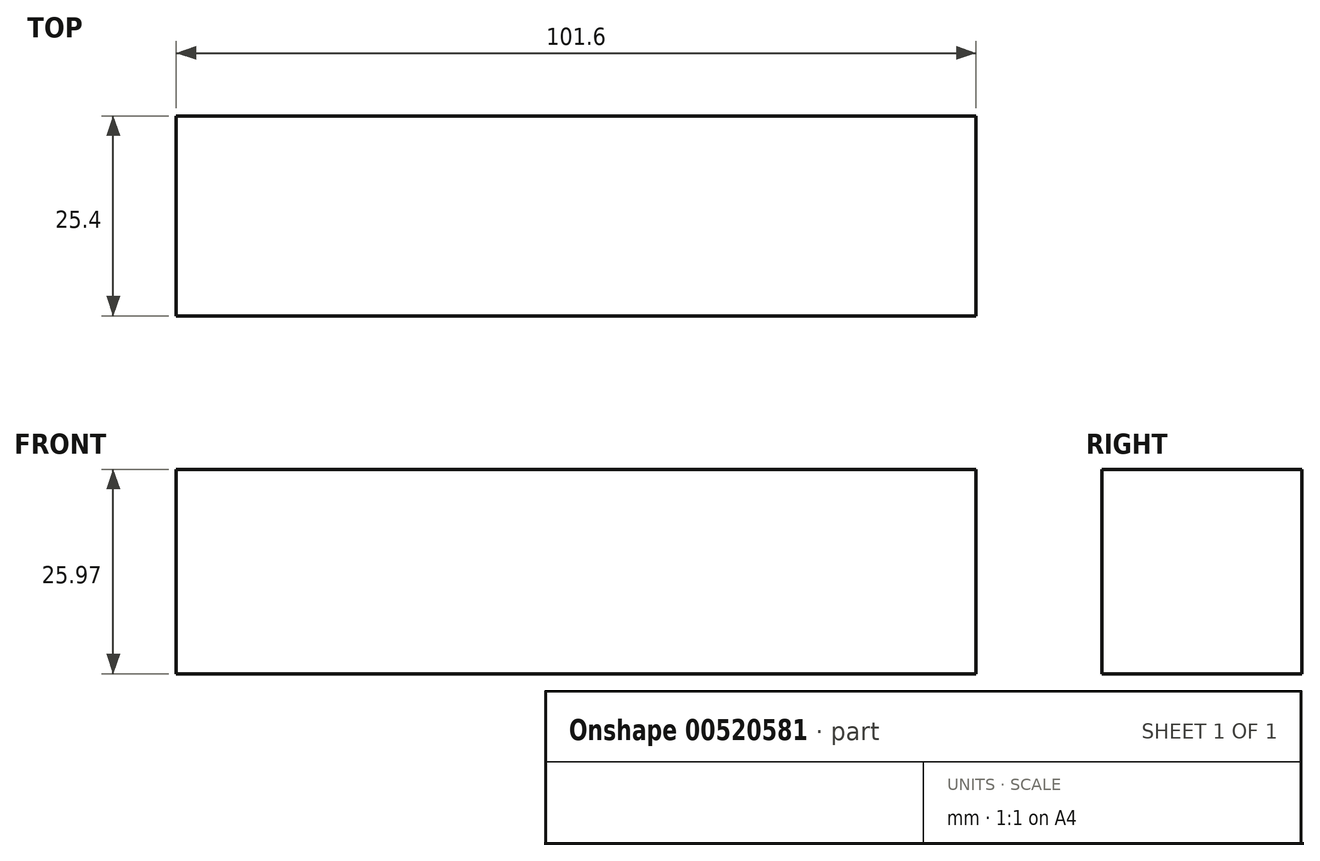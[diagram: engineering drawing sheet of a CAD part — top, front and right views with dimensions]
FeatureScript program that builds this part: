
annotation { "Feature Type Name" : "Feature", "Feature Type Description" : "" }
export const myFeature = defineFeature(function(context is Context, id is Id, definition is map)
    precondition{}
    {
        {
            var Q0;
            Q0=qCreatedBy(makeId("Front.planeOp"),FACE);
            var sketch = newSketch(context, id + "F0", { "sketchPlane" : qUnion([Q0])});
            skLineSegment(sketch, "E0", {"start": v(0, 0) * mm, "end": v(101.6, 0) * mm});
            skLineSegment(sketch, "E1", {"start": v(101.6, 0) * mm, "end": v(101.6, 101.6) * mm});
            skLineSegment(sketch, "E2", {"start": v(101.6, 101.6) * mm, "end": v(0, 101.6) * mm});
            skLineSegment(sketch, "E3", {"start": v(0, 101.6) * mm, "end": v(0, 0) * mm});
            skLineSegment(sketch, "E4", {"start": v(0, 27.93) * mm, "end": v(101.6, 27.93) * mm});
            skLineSegment(sketch, "E5", {"start": v(101.6, 27.93) * mm, "end": v(101.6, 75.63) * mm});
            skLineSegment(sketch, "E6", {"start": v(101.6, 75.63) * mm, "end": v(0, 75.63) * mm});
            skSolve(sketch);
        }
        {
            var Q0;
            {var subQ0=sQuery(id+"F0.wireOp",EDGE,"E2");Q0=makeQuery(id+"F0.imprint","IMPRINT",FACE,{"disambiguationData":[TD([[makeQuery(id+"F0.imprint","IMPRINT",EDGE,{"derivedFrom":subQ0}),1.0]])]});}
            extrude(context, id + "F1", {"entities" : qUnion([Q0]), "depth" : 25.4 * mm, "offsetDistance" : 25.4 * mm});
        }
    });
